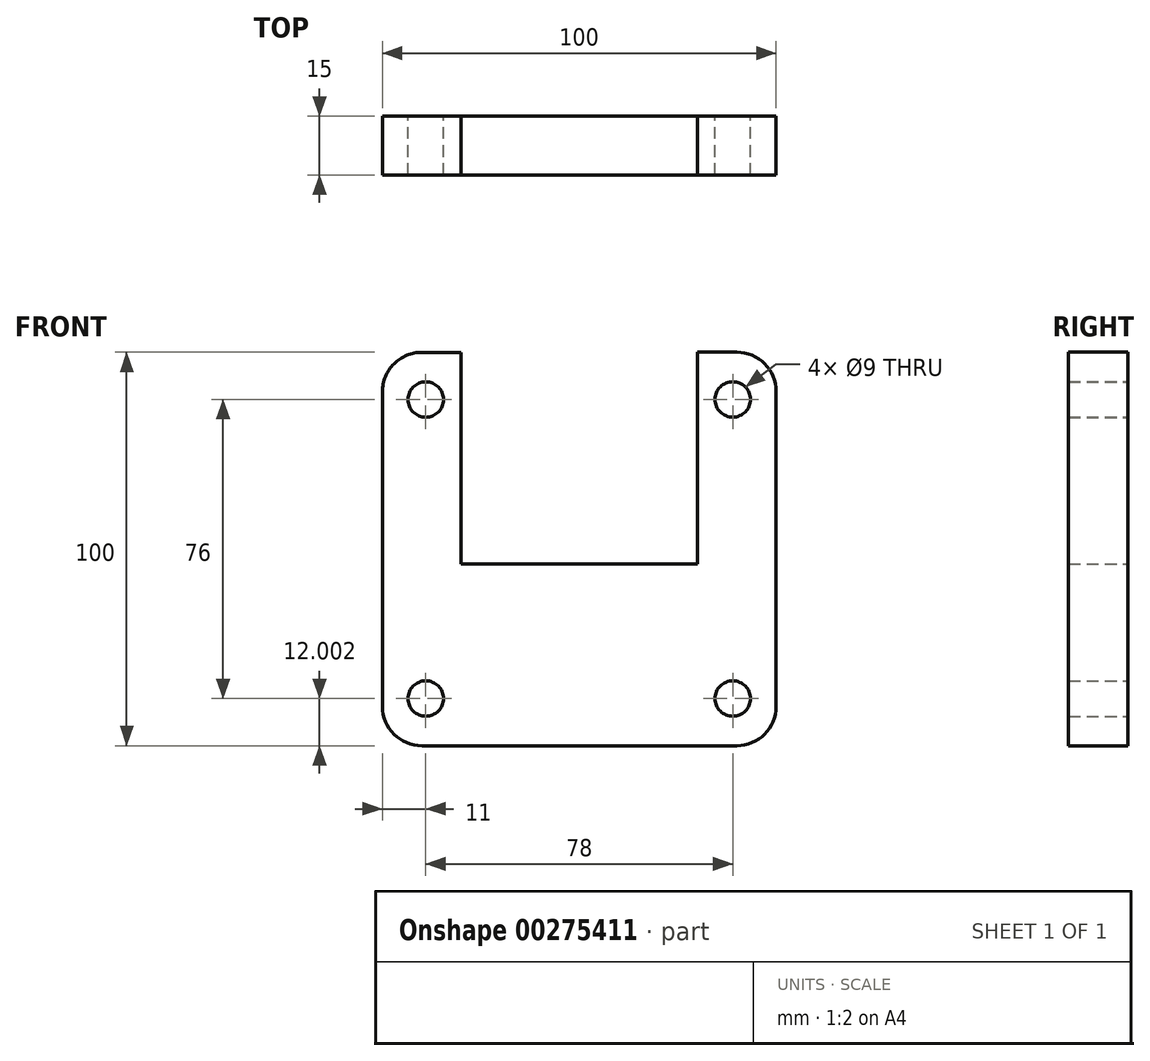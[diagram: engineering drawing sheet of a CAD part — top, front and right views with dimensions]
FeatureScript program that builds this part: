
annotation { "Feature Type Name" : "Feature", "Feature Type Description" : "" }
export const myFeature = defineFeature(function(context is Context, id is Id, definition is map)
    precondition{}
    {
        {
            var Q0;
            Q0=qCreatedBy(makeId("Front.planeOp"),FACE);
            var sketch = newSketch(context, id + "F0", { "sketchPlane" : qUnion([Q0])});
            skLineSegment(sketch, "E0.top", {"start": v(-40, -55.54) * mm, "end": v(40, -55.54) * mm});
            skPoint(sketch, "E1.visualSharp", {"position": v(54, -55.54) * mm});
            skLineSegment(sketch, "E1.filletArc", {"start": v(50, -55.54) * mm, "end": v(50, -55.54) * mm});
            skPoint(sketch, "E2.visualSharp", {"position": v(-46, -55.54) * mm});
            skLineSegment(sketch, "E2.filletArc", {"start": v(-50, -55.54) * mm, "end": v(-50, -55.54) * mm});
            skLineSegment(sketch, "E3", {"start": v(-50, 34.43) * mm, "end": v(-50, -45.54) * mm});
            skLineSegment(sketch, "E4", {"start": v(50, 34.46) * mm, "end": v(50, -45.54) * mm});
            skArc(sketch, "E5.filletArc", {"start": v(-50, -45.54) * mm, "mid": v(-47.07, -52.6) * mm, "end": v(-40, -55.54) * mm});
            skArc(sketch, "E6.filletArc", {"start": v(40, -55.54) * mm, "mid": v(47.07, -52.6) * mm, "end": v(50, -45.54) * mm});
            skLineSegment(sketch, "E7.left", {"start": v(-30, 44.4) * mm, "end": v(-30, -9.3) * mm});
            skLineSegment(sketch, "E7.right", {"start": v(30, 35.6) * mm, "end": v(30, -9.3) * mm});
            skLineSegment(sketch, "E8", {"start": v(-30, -9.3) * mm, "end": v(30, -9.3) * mm});
            skLineSegment(sketch, "E9", {"start": v(-30, 44.4) * mm, "end": v(-39.97, 44.43) * mm});
            skLineSegment(sketch, "E10", {"start": v(40, 44.46) * mm, "end": v(30, 44.46) * mm});
            skLineSegment(sketch, "E11", {"start": v(30, 44.46) * mm, "end": v(30, 35.6) * mm});
            skPoint(sketch, "E12.visualSharp", {"position": v(-50, 44.46) * mm});
            skArc(sketch, "E12.filletArc", {"start": v(-39.97, 44.43) * mm, "mid": v(-47.06, 41.51) * mm, "end": v(-50, 34.43) * mm});
            skPoint(sketch, "E13.visualSharp", {"position": v(50, 44.46) * mm});
            skArc(sketch, "E13.filletArc", {"start": v(50, 34.46) * mm, "mid": v(47.07, 41.53) * mm, "end": v(40, 44.46) * mm});
            skCircle(sketch, "E14", {"center": v(-39, -43.54) * mm, "radius": 4.5 * mm});
            skCircle(sketch, "E15", {"center": v(-39, 32.43) * mm, "radius": 4.5 * mm});
            skCircle(sketch, "E16", {"center": v(39, 32.46) * mm, "radius": 4.5 * mm});
            skCircle(sketch, "E17", {"center": v(39, -43.54) * mm, "radius": 4.5 * mm});
            skSolve(sketch);
        }
        {
            var Q0;
            Q0=makeQuery(id+"F0.imprint","IMPRINT",FACE,{"disambiguationData":[TD([[makeQuery(id+"F0.imprint","IMPRINT",EDGE,{"derivedFrom":sQuery(id+"F0.wireOp",EDGE,"E0.top")}),1.0]])]});
            extrude(context, id + "F1", {"entities" : qUnion([Q0]), "depth" : 15 * mm, "offsetDistance" : 25 * mm});
        }
    });
